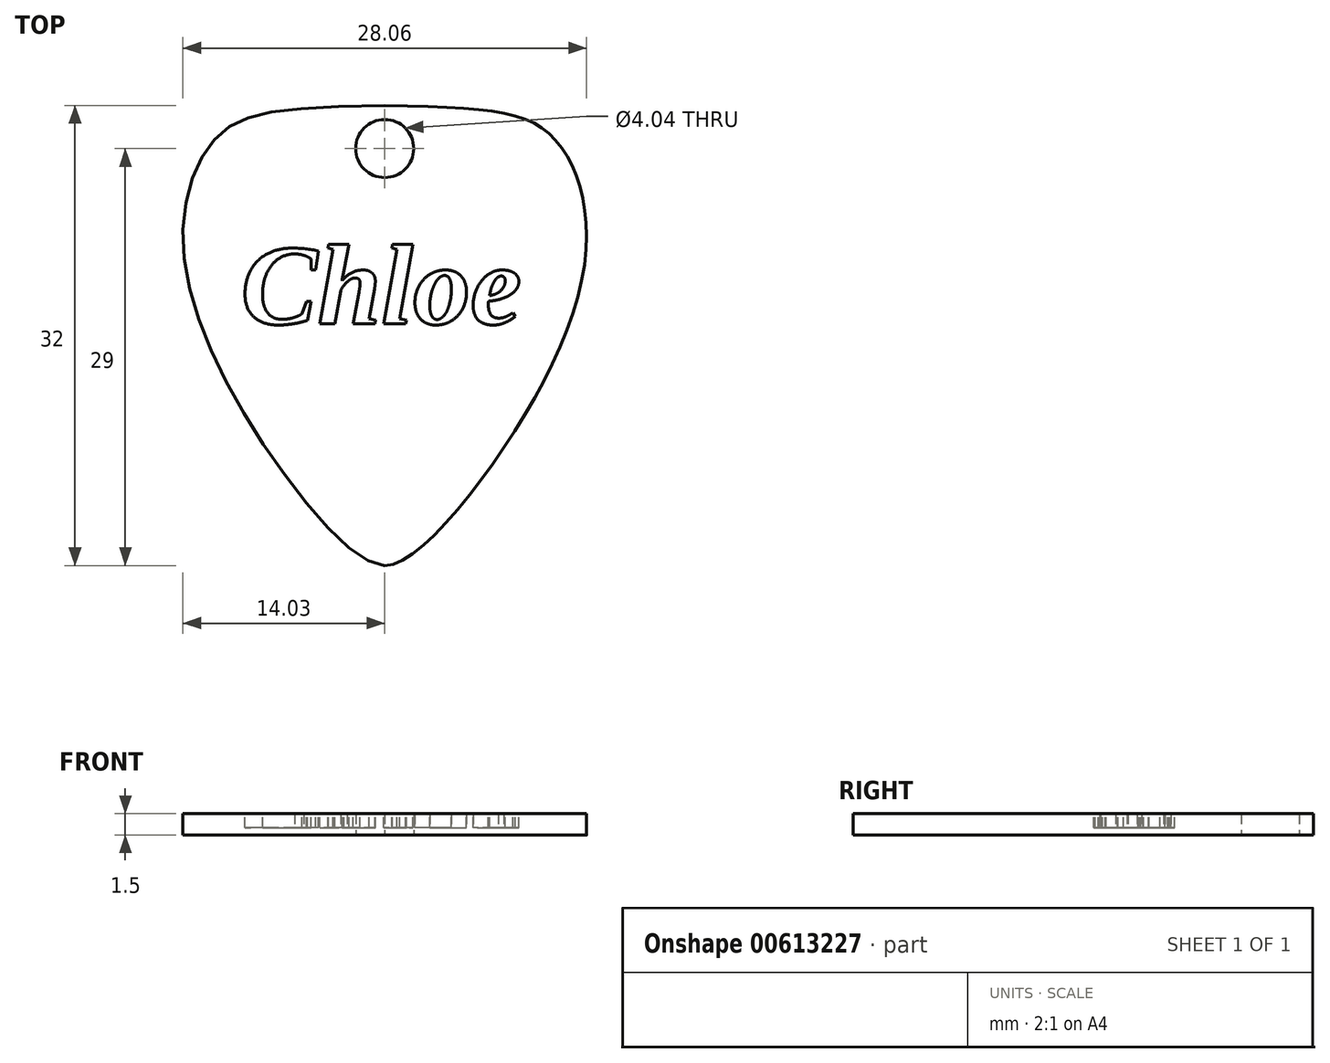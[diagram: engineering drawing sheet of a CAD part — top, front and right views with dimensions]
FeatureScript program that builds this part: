
annotation { "Feature Type Name" : "Feature", "Feature Type Description" : "" }
export const myFeature = defineFeature(function(context is Context, id is Id, definition is map)
    precondition{}
    {
        {
            var Q0;
            Q0=qCreatedBy(makeId("Top.planeOp"),FACE);
            var sketch = newSketch(context, id + "F0", { "sketchPlane" : qUnion([Q0])});
            skLineSegment(sketch, "E0", {"start": v(0, 0) * mm, "end": v(0, 32) * mm});
            skLineSegment(sketch, "E1", {"start": v(0, 0) * mm, "end": v(0, 22) * mm});
            skLineSegment(sketch, "E2", {"start": v(0, 22) * mm, "end": v(14, 22) * mm});
            skFitSpline(sketch, "E3", {"points": [v(0, 0) * mm, v(7.88, 7.6) * mm, v(14, 22) * mm, v(11.7, 29.77) * mm, v(0, 32) * mm], "startDerivative": vector(23.76, 0) * mm, "endDerivative": vector(-81.77, 1.9) * mm});
            skFitSpline(sketch, "E4.MirrorCS", {"points": [v(0, 0) * mm, v(-7.88, 7.6) * mm, v(-14, 22) * mm, v(-11.7, 29.77) * mm, v(0, 32) * mm], "startDerivative": vector(-23.76, 0) * mm, "endDerivative": vector(81.77, 1.9) * mm});
            skLineSegment(sketch, "E5", {"start": v(0, 32) * mm, "end": v(0, 29) * mm});
            skCircle(sketch, "E6", {"center": v(0, 29) * mm, "radius": 2.02 * mm});
            skSolve(sketch);
        }
        {
            var Q0;
            Q0 = qSketchRegion(id + "F0", true);
            extrude(context, id + "F1", {"entities" : qUnion([Q0]), "depth" : 1.5 * mm, "offsetDistance" : 25.4 * mm});
        }
        {
            var Q0;
            Q0=makeQuery(id+"F1.opExtrude","CAP_FACE",FACE,{"disambiguationData":[OSD([sQuery(id+"F0.wireOp",EDGE,"E3"),sQuery(id+"F0.wireOp",EDGE,"E4.MirrorCS"),sQuery(id+"F0.wireOp",EDGE,"E6")])],"isStart":false});
            var sketch = newSketch(context, id + "F2", { "sketchPlane" : qUnion([Q0])});
            skText(sketch, "E7", { "text": "Chloe", "fontName": "Tinos-BoldItalic.ttf"});
            const initialGuessF2  = {"E7": [-0.00999, 0.0168, 1, 0, 0.00574]};
            skSetInitialGuess(sketch, initialGuessF2);
            skSolve(sketch);
        }
        {
            var Q0;
            Q0 = qSketchRegion(id + "F2", true);
            var Q1;
            Q1 = qSketchRegion(id + "F0", true);
            extrude(context, id + "F3", {"entities" : qUnion([Q0, Q1]), "operationType" : NewBodyOperationType.REMOVE, "oppositeDirection" : true, "depth" : 1 * mm, "offsetDistance" : 25.4 * mm});
        }
    });
